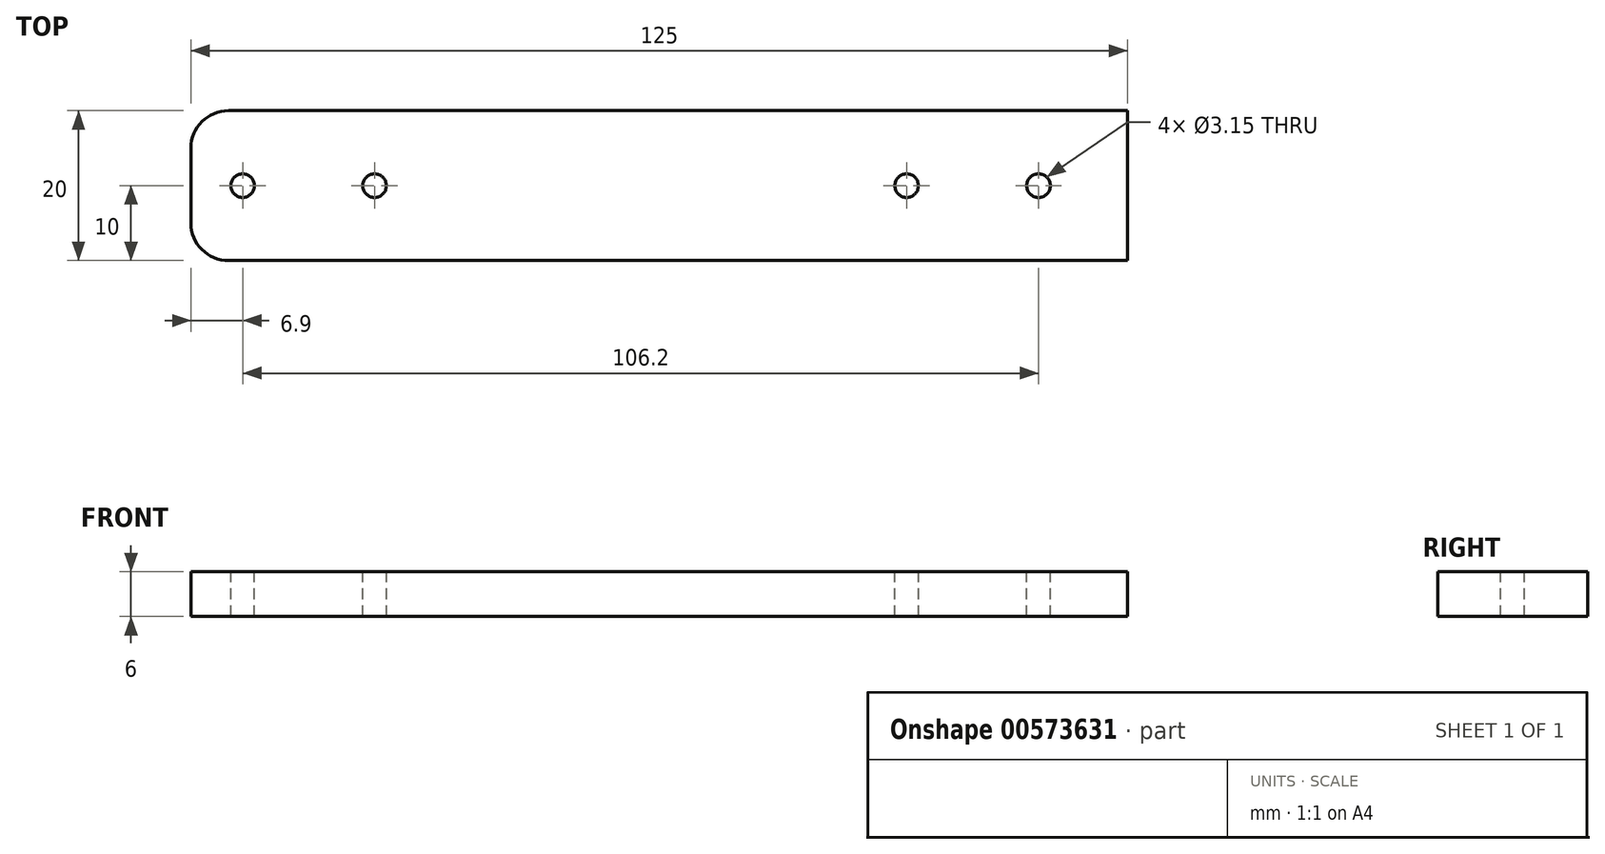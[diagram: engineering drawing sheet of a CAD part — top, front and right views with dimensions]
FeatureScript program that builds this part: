
annotation { "Feature Type Name" : "Feature", "Feature Type Description" : "" }
export const myFeature = defineFeature(function(context is Context, id is Id, definition is map)
    precondition{}
    {
        {
            var Q0;
            Q0=qCreatedBy(makeId("Top.planeOp"),FACE);
            var sketch = newSketch(context, id + "F0", { "sketchPlane" : qUnion([Q0])});
            skLineSegment(sketch, "E0.bottom", {"start": v(60, 10) * mm, "end": v(-60, 10) * mm});
            skLineSegment(sketch, "E0.top", {"start": v(60, -10) * mm, "end": v(-60, -10) * mm});
            skLineSegment(sketch, "E0.left", {"start": v(60, 10) * mm, "end": v(60, -10) * mm});
            skLineSegment(sketch, "E0.right", {"start": v(-60, 10) * mm, "end": v(-60, -10) * mm});
            skPoint(sketch, "E0.middle", {"position": v(0, 0) * mm});
            skSolve(sketch);
        }
        {
            var Q0;
            Q0 = qSketchRegion(id + "F0", true);
            extrude(context, id + "F1", {"entities" : qUnion([Q0]), "depth" : 6 * mm, "offsetDistance" : 25 * mm});
        }
        {
            var Q0;
            Q0=makeQuery(id+"F1.opExtrude","CAP_FACE",FACE,{"disambiguationData":[OSD([sQuery(id+"F0.wireOp",EDGE,"E0.bottom"),sQuery(id+"F0.wireOp",EDGE,"E0.top"),sQuery(id+"F0.wireOp",EDGE,"E0.left"),sQuery(id+"F0.wireOp",EDGE,"E0.right")])],"isStart":false});
            var sketch = newSketch(context, id + "F2", { "sketchPlane" : qUnion([Q0])});
            skCircle(sketch, "E1", {"center": v(-53.1, 0) * mm, "radius": 1.57 * mm});
            skCircle(sketch, "E2", {"center": v(-35.5, 0) * mm, "radius": 1.57 * mm});
            skLineSegment(sketch, "E3", {"start": v(-53.1, 0) * mm, "end": v(-35.5, 0) * mm, "construction": true});
            skPoint(sketch, "E4.positionSnap0", {"position": v(-44.3, 0) * mm});
            skCircle(sketch, "E5", {"center": v(-53.1, 0) * mm, "radius": 2.3 * mm, "construction": true});
            skCircle(sketch, "E6", {"center": v(-35.5, 0) * mm, "radius": 2.3 * mm, "construction": true});
            skLineSegment(sketch, "E7", {"start": v(0, 10) * mm, "end": v(0, -10) * mm, "construction": true});
            skPoint(sketch, "E8.MirrorP", {"position": v(44.3, 0) * mm});
            skCircle(sketch, "E9.MirrorC", {"center": v(53.1, 0) * mm, "radius": 1.57 * mm});
            skCircle(sketch, "E10.MirrorC", {"center": v(35.5, 0) * mm, "radius": 1.57 * mm});
            skCircle(sketch, "E11.MirrorC", {"center": v(53.1, 0) * mm, "radius": 2.3 * mm, "construction": true});
            skCircle(sketch, "E12.MirrorC", {"center": v(35.5, 0) * mm, "radius": 2.3 * mm, "construction": true});
            skSolve(sketch);
        }
        {
            var Q0;
            Q0 = qSketchRegion(id + "F2", true);
            var Q1;
            Q1=makeQuery(id+"F1.opExtrude","CAP_FACE",FACE,{"disambiguationData":[OSD([sQuery(id+"F0.wireOp",EDGE,"E0.bottom"),sQuery(id+"F0.wireOp",EDGE,"E0.top"),sQuery(id+"F0.wireOp",EDGE,"E0.left"),sQuery(id+"F0.wireOp",EDGE,"E0.right")])],"isStart":true});
            extrude(context, id + "F3", {"entities" : qUnion([Q0]), "operationType" : NewBodyOperationType.REMOVE, "endBound" : BoundingType.UP_TO_SURFACE, "oppositeDirection" : true, "depth" : 25 * mm, "endBoundEntityFace" : qUnion([Q1]), "offsetDistance" : 25 * mm});
        }
        {
            var Q0;
            Q0=qCreatedBy(makeId("Top.planeOp"),FACE);
            var sketch = newSketch(context, id + "F4", { "sketchPlane" : qUnion([Q0])});
            skLineSegment(sketch, "E13.bottom", {"start": v(60, 10) * mm, "end": v(65, 10) * mm});
            skLineSegment(sketch, "E13.top", {"start": v(60, -10) * mm, "end": v(65, -10) * mm});
            skLineSegment(sketch, "E13.left", {"start": v(60, 10) * mm, "end": v(60, -10) * mm});
            skLineSegment(sketch, "E13.right", {"start": v(65, 10) * mm, "end": v(65, -10) * mm});
            skSolve(sketch);
        }
        {
            var Q0;
            Q0 = qSketchRegion(id + "F4", true);
            var Q1;
            Q1=makeQuery(id+"F1.opExtrude","CAP_FACE",FACE,{"disambiguationData":[OSD([sQuery(id+"F0.wireOp",EDGE,"E0.bottom"),sQuery(id+"F0.wireOp",EDGE,"E0.top"),sQuery(id+"F0.wireOp",EDGE,"E0.left"),sQuery(id+"F0.wireOp",EDGE,"E0.right")])],"isStart":false});
            extrude(context, id + "F5", {"entities" : qUnion([Q0]), "operationType" : NewBodyOperationType.ADD, "endBound" : BoundingType.UP_TO_SURFACE, "depth" : 25 * mm, "endBoundEntityFace" : qUnion([Q1]), "offsetDistance" : 25 * mm});
        }
        {
            var Q0;
            Q0=makeQuery(id+"F1.opExtrude","SWEPT_EDGE",EDGE,{"disambiguationData":[OSD([sQuery(id+"F0.wireOp",EDGE,"E0.top"),sQuery(id+"F0.wireOp",EDGE,"E0.right")])]});
            var Q1;
            Q1=makeQuery(id+"F1.opExtrude","SWEPT_EDGE",EDGE,{"disambiguationData":[OSD([sQuery(id+"F0.wireOp",EDGE,"E0.bottom"),sQuery(id+"F0.wireOp",EDGE,"E0.right")])]});
            fillet(context, id + "F6", {"entities" : qUnion([Q0, Q1]), "radius" : 5 * mm, "tangentPropagation" : true, "allowEdgeOverflow" : false});
        }
    });
